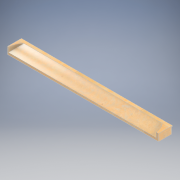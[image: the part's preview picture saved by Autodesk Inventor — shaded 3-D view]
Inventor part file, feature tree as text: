
AUTODESK INVENTOR PART (.ipt)
format: ipt  version: 2022.2 (Build 262287010, 287A)  size: 204,288 bytes
history: native  units: in
note: dims shown in document units (in); Inventor stores cm internally (conversion verified against a paired STEP export)
features: revolve x2, direct_edit x1, extrude x1, sketch x1, projected_geometry x1
ambient origin geometry x8: Origin, YZ Plane, XZ Plane, XY Plane, X Axis, Y Axis, Z Axis, Center Point
bodies: Solid1 (feature_tree), Body1 (feature_tree)
feature tree (6):
  direct_edit  "Direct Edit1"
  extrude  "Extrusion1"  [1 undecoded]
  sketch  "Sketch1"  dims[d0=180.0deg d1=-0.6184in d2=0.375in d3=0.0in]
  projected_geometry  "Projected Loop1"
  revolve  "Rotate1"  [1 undecoded]
  revolve  "Rotate2"  [1 undecoded]
note: 3 required parameter values undecoded (feature->parameter linkage not recoverable at this tier; creation-order binding heuristic only, values carry confidence <= 0.55)